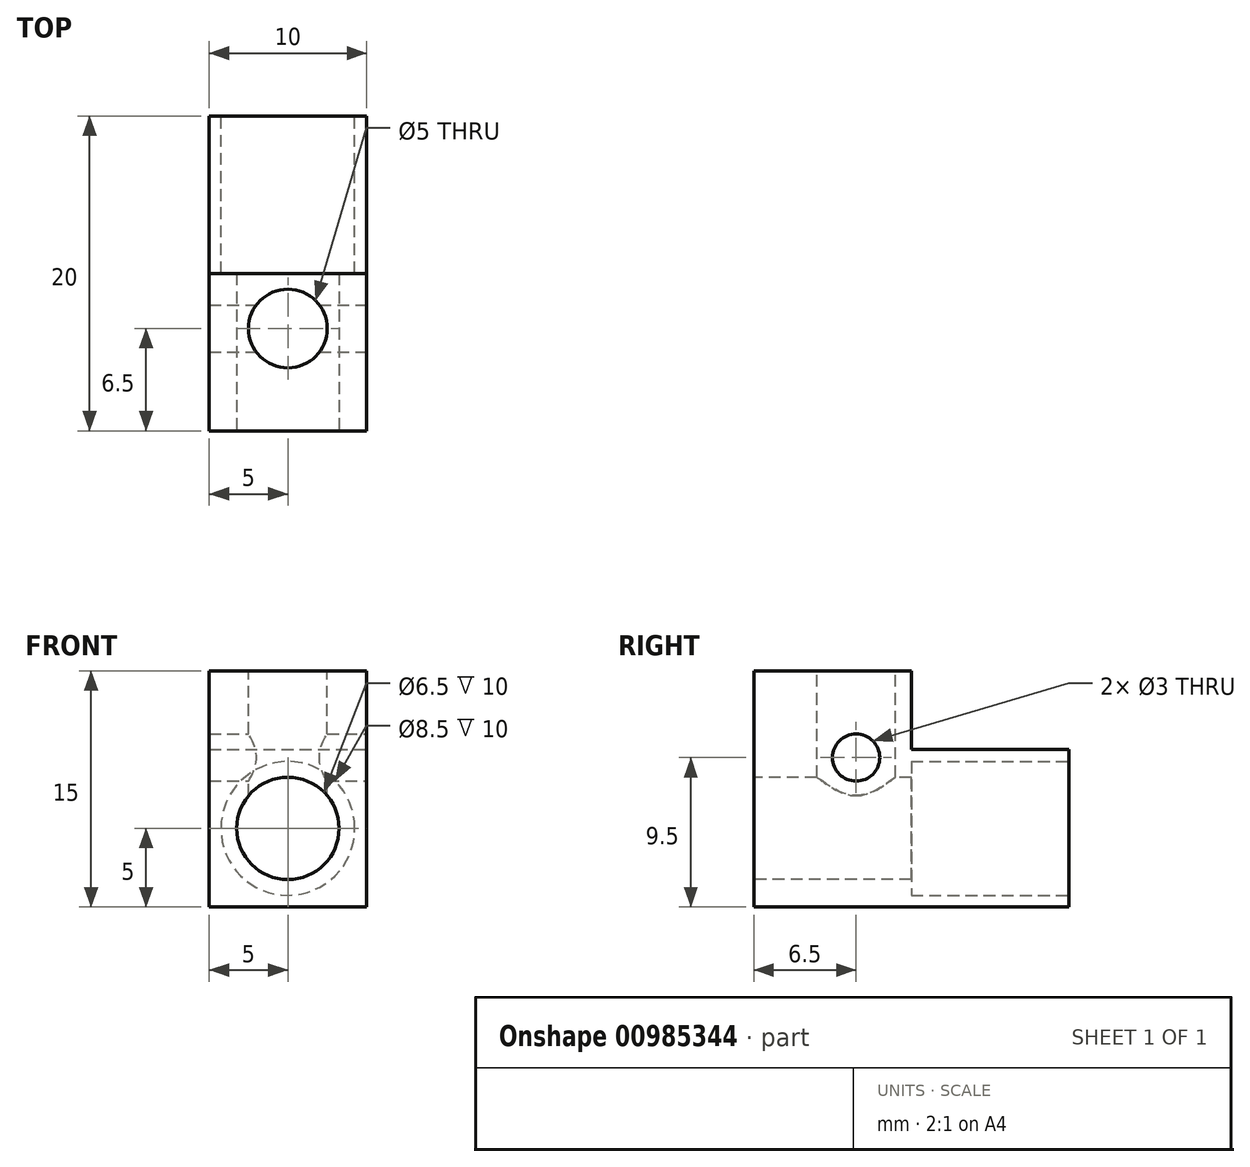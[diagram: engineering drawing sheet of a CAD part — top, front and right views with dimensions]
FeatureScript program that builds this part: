
annotation { "Feature Type Name" : "Feature", "Feature Type Description" : "" }
export const myFeature = defineFeature(function(context is Context, id is Id, definition is map)
    precondition{}
    {
        {
            var Q0;
            Q0=qCreatedBy(makeId("Front.planeOp"),FACE);
            var sketch = newSketch(context, id + "F0", { "sketchPlane" : qUnion([Q0])});
            skCircle(sketch, "E0", {"center": v(0, 0) * mm, "radius": 3.25 * mm});
            skLineSegment(sketch, "E1.bottom", {"start": v(5, -5) * mm, "end": v(-5, -5) * mm});
            skLineSegment(sketch, "E1.top", {"start": v(5, 10) * mm, "end": v(-5, 10) * mm});
            skLineSegment(sketch, "E1.left", {"start": v(5, -5) * mm, "end": v(5, 10) * mm});
            skLineSegment(sketch, "E1.right", {"start": v(-5, -5) * mm, "end": v(-5, 10) * mm});
            skPoint(sketch, "E1.middle", {"position": v(0, 2.5) * mm});
            skLineSegment(sketch, "E2", {"start": v(-5, 5) * mm, "end": v(5, 5) * mm});
            skPoint(sketch, "E2.endSnap0", {"position": v(5, 2.5) * mm});
            skSolve(sketch);
        }
        {
            var Q0;
            Q0=makeQuery(id+"F0.imprint","IMPRINT",FACE,{"disambiguationData":[TD([[makeQuery(id+"F0.imprint","IMPRINT",EDGE,{"derivedFrom":sQuery(id+"F0.wireOp",EDGE,"E0")}),-1.0]])]});
            extrude(context, id + "F1", {"entities" : qUnion([Q0]), "oppositeDirection" : true, "depth" : 10 * mm});
        }
        {
            var Q0;
            {var subQ0=sQuery(id+"F0.wireOp",EDGE,"E1.top");Q0=makeQuery(id+"F0.imprint","IMPRINT",FACE,{"disambiguationData":[TD([[makeQuery(id+"F0.imprint","IMPRINT",EDGE,{"derivedFrom":subQ0}),1.0]])]});}
            var Q1;
            Q1=makeQuery(id+"F0.imprint","IMPRINT",FACE,{"disambiguationData":[TD([[makeQuery(id+"F0.imprint","IMPRINT",EDGE,{"derivedFrom":sQuery(id+"F0.wireOp",EDGE,"E0")}),-1.0]])]});
            extrude(context, id + "F2", {"entities" : qUnion([Q0, Q1]), "operationType" : NewBodyOperationType.ADD, "depth" : 10 * mm});
        }
        {
            var Q0;
            Q0=makeQuery(id+"F1.opExtrude","CAP_FACE",FACE,{"disambiguationData":[OSD([sQuery(id+"F0.wireOp",EDGE,"E0"),sQuery(id+"F0.wireOp",EDGE,"E1.bottom"),sQuery(id+"F0.wireOp",EDGE,"E1.left"),sQuery(id+"F0.wireOp",EDGE,"E1.right"),sQuery(id+"F0.wireOp",EDGE,"E2")])],"isStart":false});
            var sketch = newSketch(context, id + "F3", { "sketchPlane" : qUnion([Q0])});
            skCircle(sketch, "E3", {"center": v(0, 0) * mm, "radius": 4.25 * mm});
            skSolve(sketch);
        }
        {
            var Q0;
            Q0=makeQuery(id+"F3.imprint","IMPRINT",FACE,{"disambiguationData":[TD([[makeQuery(id+"F3.imprint","IMPRINT",EDGE,{"derivedFrom":makeQuery(id+"F1.opExtrude","CAP_EDGE",EDGE,{"disambiguationData":[OSD([sQuery(id+"F0.wireOp",EDGE,"E0")])],"isStart":false})}),1.0]])]});
            extrude(context, id + "F4", {"entities" : qUnion([Q0]), "operationType" : NewBodyOperationType.REMOVE, "oppositeDirection" : true, "depth" : 10 * mm});
        }
        {
            var Q0;
            Q0=qCreatedBy(makeId("Right.planeOp"),FACE);
            var sketch = newSketch(context, id + "F5", { "sketchPlane" : qUnion([Q0])});
            skCircle(sketch, "E4", {"center": v(-3.5, 4.5) * mm, "radius": 1.5 * mm});
            skLineSegment(sketch, "E5", {"start": v(0, 3) * mm, "end": v(-10, 3) * mm, "construction": true});
            skSolve(sketch);
        }
        {
            var Q0;
            Q0=makeQuery(id+"F5.imprint","IMPRINT",FACE,{"disambiguationData":[TD([[makeQuery(id+"F5.imprint","IMPRINT",EDGE,{"derivedFrom":sQuery(id+"F5.wireOp",EDGE,"E4")}),1.0]])]});
            extrude(context, id + "F6", {"entities" : qUnion([Q0]), "operationType" : NewBodyOperationType.REMOVE, "endBound" : BoundingType.THROUGH_ALL, "oppositeDirection" : true, "depth" : 25 * mm, "hasSecondDirection" : true, "secondDirectionBound" : SecondDirectionBoundingType.THROUGH_ALL, "secondDirectionOppositeDirection" : false, "secondDirectionDepth" : 25 * mm});
        }
        {
            var Q0;
            Q0=makeQuery(id+"F2.opExtrude","SWEPT_FACE",FACE,{"disambiguationData":[OSD([sQuery(id+"F0.wireOp",EDGE,"E1.top")])]});
            var sketch = newSketch(context, id + "F7", { "sketchPlane" : qUnion([Q0])});
            skCircle(sketch, "E6", {"center": v(0, -3.5) * mm, "radius": 2.5 * mm});
            skSolve(sketch);
        }
        {
            var Q0;
            Q0=makeQuery(id+"F7.imprint","IMPRINT",FACE,{"disambiguationData":[TD([[makeQuery(id+"F7.imprint","IMPRINT",EDGE,{"derivedFrom":sQuery(id+"F7.wireOp",EDGE,"E6")}),1.0]])]});
            extrude(context, id + "F8", {"entities" : qUnion([Q0]), "operationType" : NewBodyOperationType.REMOVE, "oppositeDirection" : true, "depth" : 10 * mm});
        }
    });
